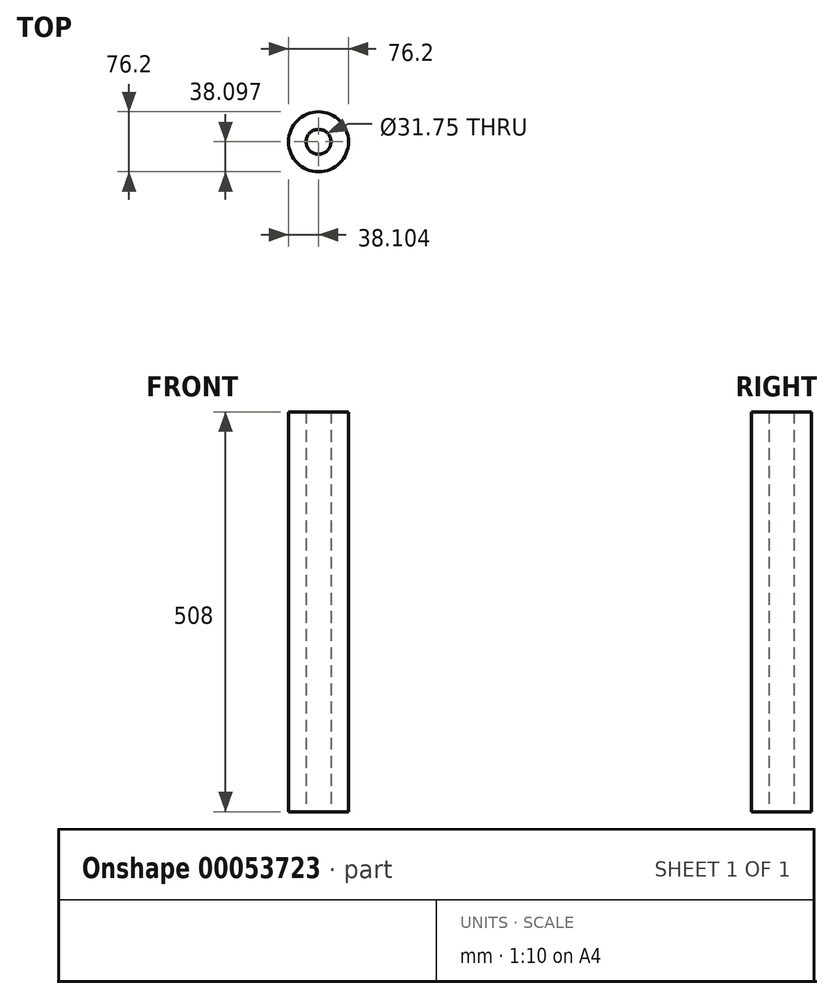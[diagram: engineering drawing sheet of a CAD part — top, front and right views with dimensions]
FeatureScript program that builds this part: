
annotation { "Feature Type Name" : "Feature", "Feature Type Description" : "" }
export const myFeature = defineFeature(function(context is Context, id is Id, definition is map)
    precondition{}
    {
        {
            var Q0;
            Q0=qCreatedBy(makeId("Top.planeOp"),FACE);
            var sketch = newSketch(context, id + "F0", { "sketchPlane" : qUnion([Q0])});
            skCircle(sketch, "E0", {"center": v(-11.03, 6.4) * mm, "radius": 38.1 * mm});
            skCircle(sketch, "E1", {"center": v(-11.03, 6.4) * mm, "radius": 15.88 * mm});
            skSolve(sketch);
        }
        {
            var Q0;
            Q0 = qSketchRegion(id + "F0", true);
            extrude(context, id + "F1", {"entities" : qUnion([Q0]), "depth" : 508 * mm});
        }
    });
